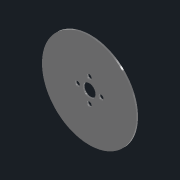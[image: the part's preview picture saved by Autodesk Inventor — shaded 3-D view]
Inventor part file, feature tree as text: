
AUTODESK INVENTOR PART (.ipt)
format: ipt  version: 2022.2 (Build 262287010, 287A)  size: 96,256 bytes
history: native  units: mm
features: sketch x3, hole x2, extrude x1
ambient origin geometry x8: Origin, YZ Plane, XZ Plane, XY Plane, X Axis, Y Axis, Z Axis, Center Point
bodies: Solid1 (feature_tree)
feature tree (6):
  extrude  "Extrusion1"  Depth=1.0mm TaperAngle=0.0deg
  hole  "Hole1"  [1 undecoded]
  hole  "Hole2"  [1 undecoded]
  sketch  "Sketch1"  dims[d0=60.0mm d1=1.0mm d2=0.0mm]
  sketch  "Sketch2"  dims[d3=8.0mm d4=6.0mm d5=4.0mm d6=2.0mm d7=90.0deg d8=8.0mm d9=20.594885mm d10=15.0mm]
  sketch  "Sketch3"  dims[d11=3.0mm d12=6.0mm d13=4.0mm d14=2.0mm d15=90.0deg d16=8.0mm d17=20.594885mm]
note: 2 required parameter values undecoded (feature->parameter linkage not recoverable at this tier; creation-order binding heuristic only, values carry confidence <= 0.55)
